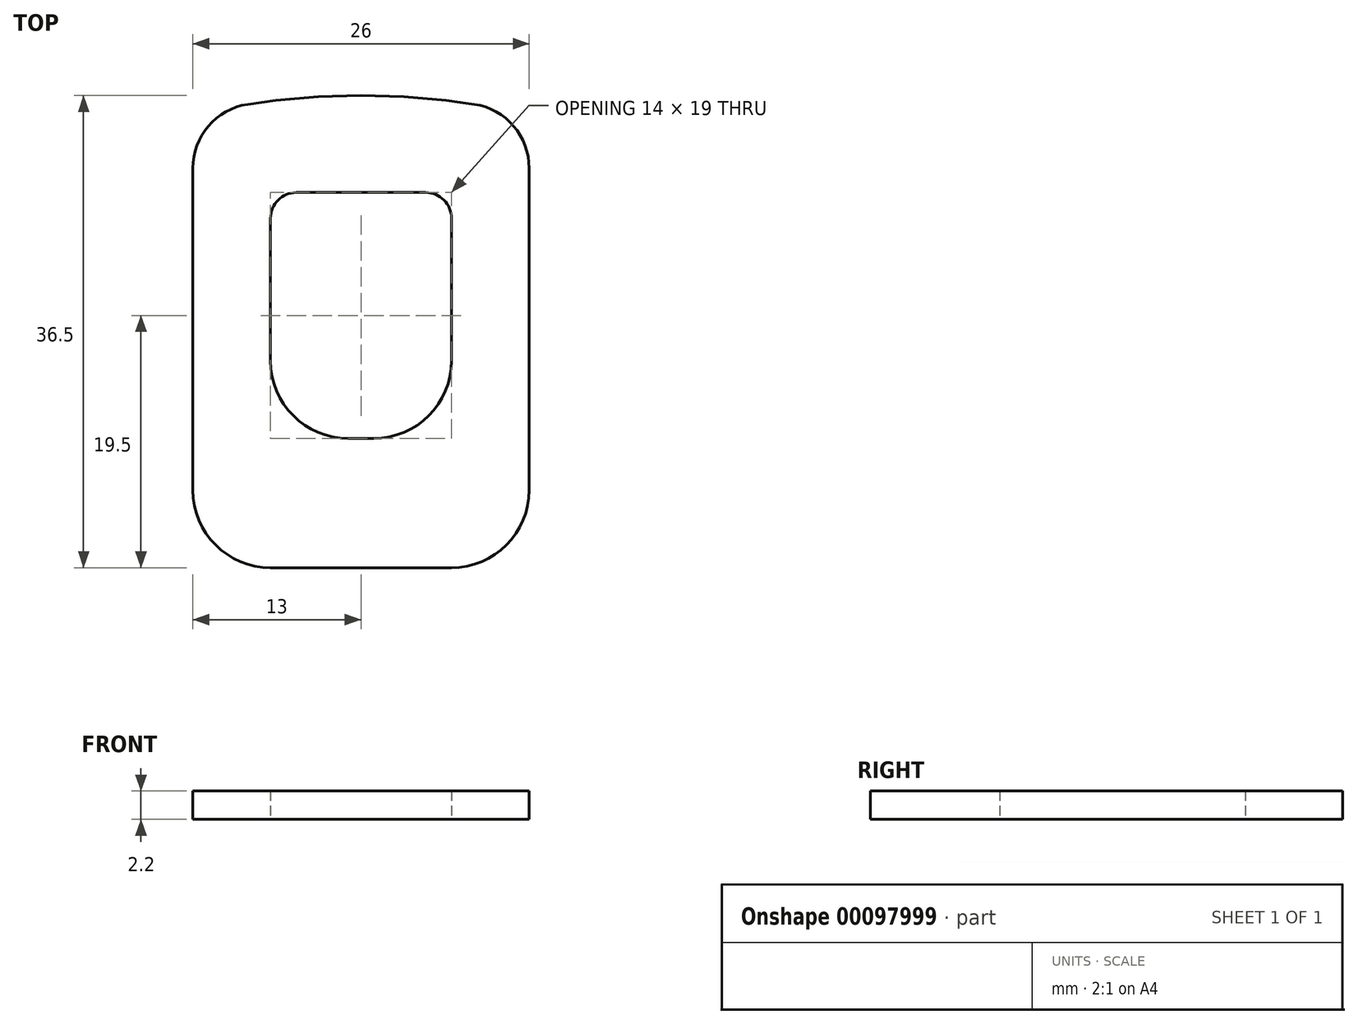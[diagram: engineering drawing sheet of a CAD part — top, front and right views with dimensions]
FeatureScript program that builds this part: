
annotation { "Feature Type Name" : "Feature", "Feature Type Description" : "" }
export const myFeature = defineFeature(function(context is Context, id is Id, definition is map)
    precondition{}
    {
        {
            var Q0;
            Q0=qCreatedBy(makeId("Top.planeOp"),FACE);
            var sketch = newSketch(context, id + "F0", { "sketchPlane" : qUnion([Q0])});
            skLineSegment(sketch, "E0.bottom", {"start": v(6, 0) * mm, "end": v(20, 0) * mm});
            skLineSegment(sketch, "E0.left", {"start": v(0, 6) * mm, "end": v(0, 30.88) * mm});
            skLineSegment(sketch, "E0.right", {"start": v(26, 6) * mm, "end": v(26, 30.88) * mm});
            skLineSegment(sketch, "E1.bottom", {"start": v(8, 29) * mm, "end": v(18, 29) * mm});
            skLineSegment(sketch, "E1.top", {"start": v(12, 10) * mm, "end": v(14, 10) * mm});
            skLineSegment(sketch, "E1.left", {"start": v(6, 27) * mm, "end": v(6, 16) * mm});
            skLineSegment(sketch, "E1.right", {"start": v(20, 27) * mm, "end": v(20, 16) * mm});
            skPoint(sketch, "E2.visualSharp", {"position": v(0, 35) * mm});
            skPoint(sketch, "E3.visualSharp", {"position": v(26, 35) * mm});
            skPoint(sketch, "E4.visualSharp", {"position": v(0, 0) * mm});
            skArc(sketch, "E4.filletArc", {"start": v(0, 6) * mm, "mid": v(1.76, 1.76) * mm, "end": v(6, 0) * mm});
            skPoint(sketch, "E5.visualSharp", {"position": v(26, 0) * mm});
            skArc(sketch, "E5.filletArc", {"start": v(20, 0) * mm, "mid": v(24.24, 1.76) * mm, "end": v(26, 6) * mm});
            skPoint(sketch, "E6.visualSharp", {"position": v(6, 10) * mm});
            skArc(sketch, "E6.filletArc", {"start": v(6, 16) * mm, "mid": v(7.76, 11.76) * mm, "end": v(12, 10) * mm});
            skPoint(sketch, "E7.visualSharp", {"position": v(20, 10) * mm});
            skArc(sketch, "E7.filletArc", {"start": v(14, 10) * mm, "mid": v(18.24, 11.76) * mm, "end": v(20, 16) * mm});
            skPoint(sketch, "E8.visualSharp", {"position": v(20, 29) * mm});
            skArc(sketch, "E8.filletArc", {"start": v(20, 27) * mm, "mid": v(19.41, 28.41) * mm, "end": v(18, 29) * mm});
            skPoint(sketch, "E9.visualSharp", {"position": v(6, 29) * mm});
            skArc(sketch, "E9.filletArc", {"start": v(8, 29) * mm, "mid": v(6.59, 28.41) * mm, "end": v(6, 27) * mm});
            skArc(sketch, "E10", {"start": v(21.77, 35.82) * mm, "mid": v(13, 36.5) * mm, "end": v(4.23, 35.82) * mm});
            skArc(sketch, "E11.filletArc", {"start": v(4.23, 35.82) * mm, "mid": v(1.2, 34.13) * mm, "end": v(0, 30.88) * mm});
            skArc(sketch, "E12.filletArc", {"start": v(26, 30.88) * mm, "mid": v(24.8, 34.13) * mm, "end": v(21.77, 35.82) * mm});
            skSolve(sketch);
        }
        {
            var Q0;
            Q0=makeQuery(id+"F0.imprint","IMPRINT",FACE,{"disambiguationData":[TD([[makeQuery(id+"F0.imprint","IMPRINT",EDGE,{"derivedFrom":sQuery(id+"F0.wireOp",EDGE,"E0.bottom")}),1.0]])]});
            extrude(context, id + "F1", {"entities" : qUnion([Q0]), "depth" : 2.2 * mm});
        }
    });
